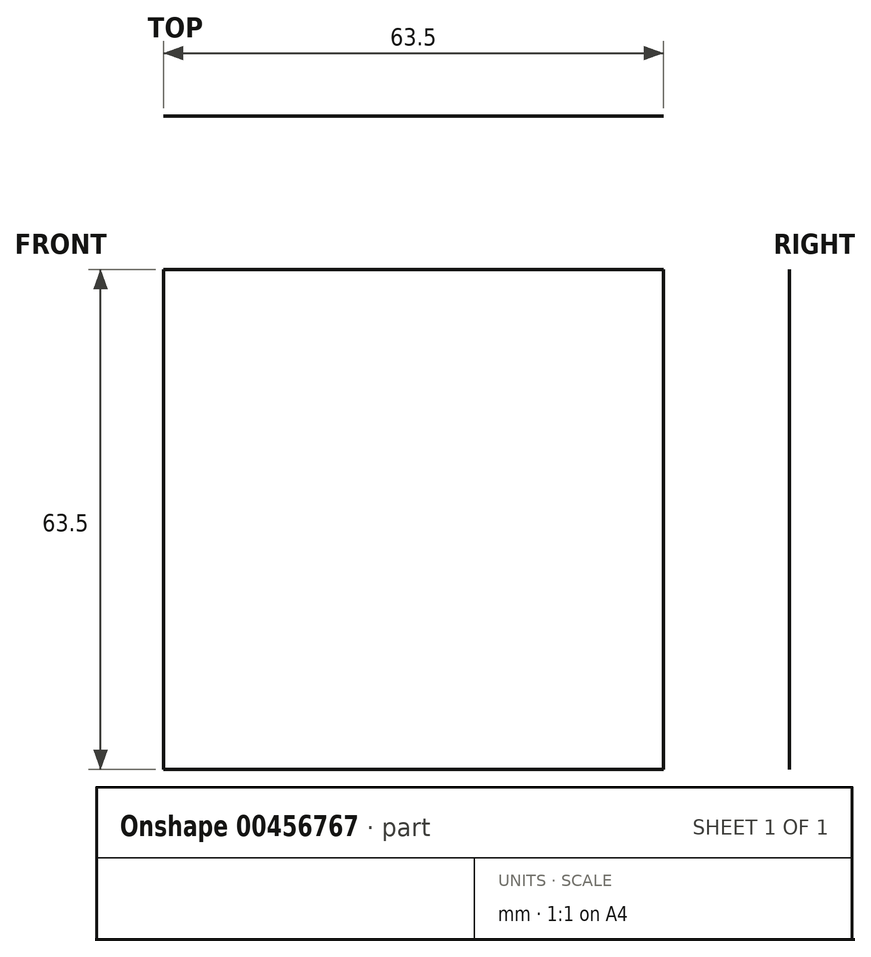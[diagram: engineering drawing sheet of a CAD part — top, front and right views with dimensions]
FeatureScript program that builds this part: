
annotation { "Feature Type Name" : "Feature", "Feature Type Description" : "" }
export const myFeature = defineFeature(function(context is Context, id is Id, definition is map)
    precondition{}
    {
        {
            var Q0;
            Q0=qCreatedBy(makeId("Front.planeOp"),FACE);
            var sketch = newSketch(context, id + "F0", { "sketchPlane" : qUnion([Q0])});
            skLineSegment(sketch, "E0.bottom", {"start": v(-31.75, 31.75) * mm, "end": v(31.75, 31.75) * mm});
            skLineSegment(sketch, "E0.top", {"start": v(-31.75, -31.75) * mm, "end": v(31.75, -31.75) * mm});
            skLineSegment(sketch, "E0.left", {"start": v(-31.75, 31.75) * mm, "end": v(-31.75, -31.75) * mm});
            skLineSegment(sketch, "E0.right", {"start": v(31.75, 31.75) * mm, "end": v(31.75, -31.75) * mm});
            skPoint(sketch, "E0.middle", {"position": v(0, 0) * mm});
            skSolve(sketch);
        }
        {
            var Q0;
            Q0=makeQuery(id+"F0.imprint","IMPRINT",FACE,{"disambiguationData":[TD([[makeQuery(id+"F0.imprint","IMPRINT",EDGE,{"derivedFrom":sQuery(id+"F0.wireOp",EDGE,"E0.bottom")}),-1.0]])]});
            extrude(context, id + "F1", {"entities" : qUnion([Q0]), "depth" : 1 / 203.2 * mm});
        }
    });
